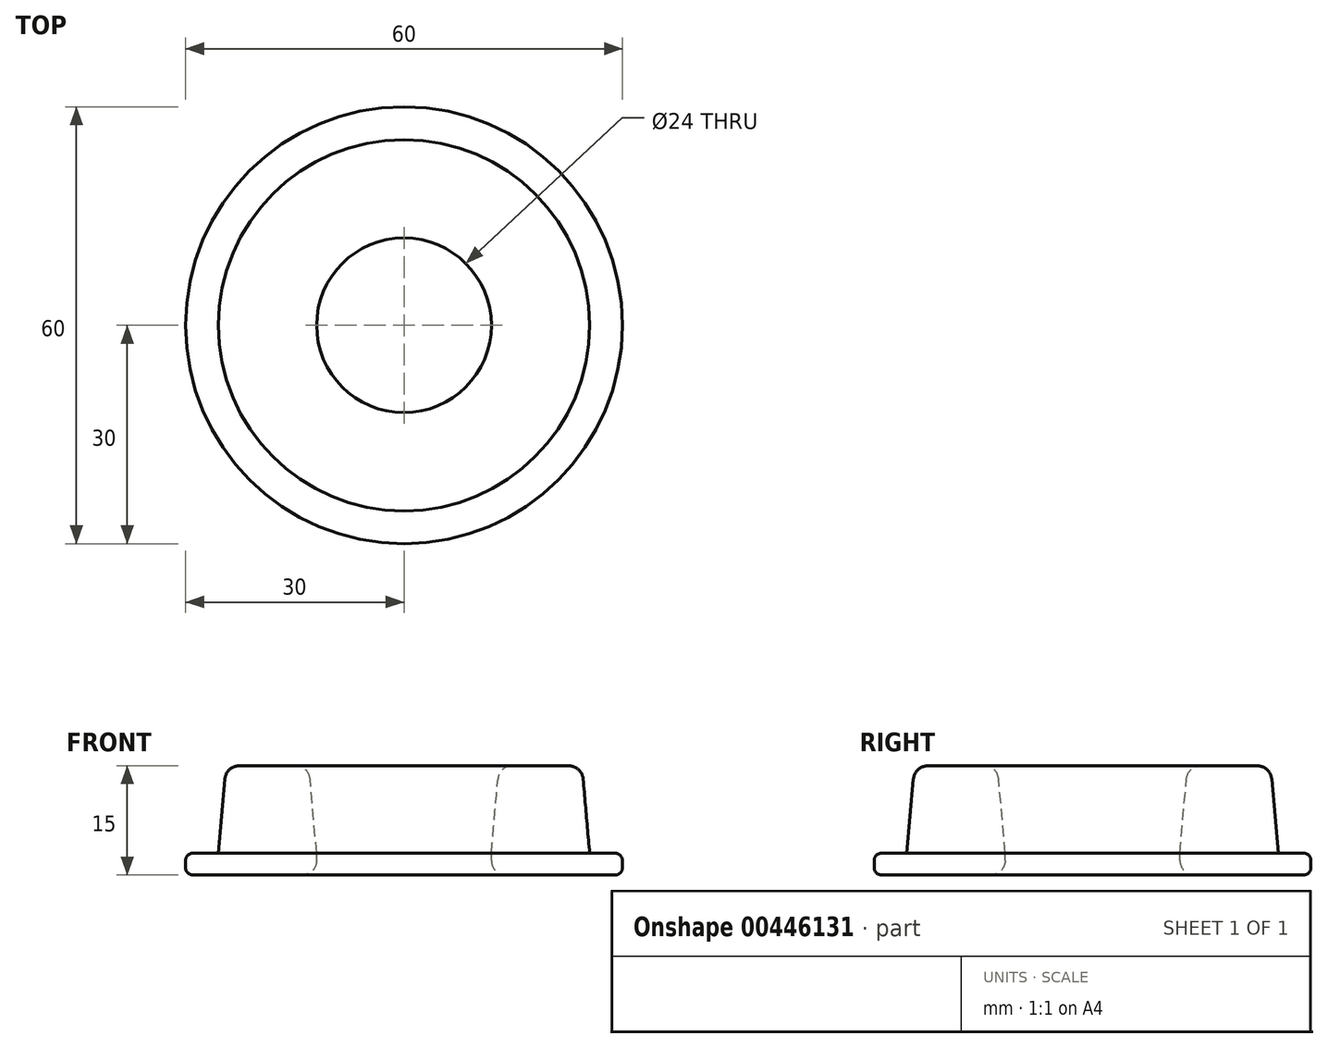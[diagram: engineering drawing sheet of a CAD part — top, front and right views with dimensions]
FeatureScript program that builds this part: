
annotation { "Feature Type Name" : "Feature", "Feature Type Description" : "" }
export const myFeature = defineFeature(function(context is Context, id is Id, definition is map)
    precondition{}
    {
        {
            var Q0;
            Q0=qCreatedBy(makeId("Top.planeOp"),FACE);
            var sketch = newSketch(context, id + "F0", { "sketchPlane" : qUnion([Q0])});
            skCircle(sketch, "E0", {"center": v(0, 0) * mm, "radius": 12 * mm});
            skCircle(sketch, "E1", {"center": v(0, 0) * mm, "radius": 25.5 * mm});
            skCircle(sketch, "E2", {"center": v(0, 0) * mm, "radius": 25.5 * mm, "construction": true});
            skSolve(sketch);
        }
        {
            var Q0;
            Q0=qSketchRegion(id+"F0",true);
            extrude(context, id + "F1", {"entities" : qUnion([Q0]), "depth" : 12 * mm, "hasDraft" : true, "draftAngle" : 5 * degree, "draftPullDirection" : true});
        }
        {
            var Q0;
            Q0=qCreatedBy(makeId("Top.planeOp"),FACE);
            var sketch = newSketch(context, id + "F2", { "sketchPlane" : qUnion([Q0])});
            skCircle(sketch, "E3", {"center": v(0, 0) * mm, "radius": 30 * mm});
            skCircle(sketch, "E4", {"center": v(0, 0) * mm, "radius": 12 * mm});
            skSolve(sketch);
        }
        {
            var Q0;
            Q0=qSketchRegion(id+"F2",true);
            extrude(context, id + "F3", {"entities" : qUnion([Q0]), "operationType" : NewBodyOperationType.ADD, "oppositeDirection" : true, "depth" : 3 * mm});
        }
        {
            var Q0;
            Q0=makeQuery(id+"F1.opExtrude","CAP_EDGE",EDGE,{"disambiguationData":[OSD([sQuery(id+"F0.wireOp",EDGE,"E1")])],"isStart":false});
            var Q1;
            Q1=makeQuery(id+"F3.opExtrude","CAP_EDGE",EDGE,{"disambiguationData":[OSD([sQuery(id+"F2.wireOp",EDGE,"E4")])],"isStart":false});
            var Q2;
            Q2=makeQuery(id+"F1.opExtrude","CAP_EDGE",EDGE,{"disambiguationData":[OSD([sQuery(id+"F0.wireOp",EDGE,"E0")])],"isStart":false});
            fillet(context, id + "F4", {"entities" : qUnion([Q0, Q1, Q2]), "radius" : 2 * mm, "tangentPropagation" : true, "allowEdgeOverflow" : false});
        }
        {
            var Q0;
            Q0=makeQuery(id+"F3.opExtrude","CAP_EDGE",EDGE,{"disambiguationData":[OSD([sQuery(id+"F2.wireOp",EDGE,"E3")])],"isStart":false});
            var Q1;
            Q1=makeQuery(id+"F3.opExtrude","CAP_EDGE",EDGE,{"disambiguationData":[OSD([sQuery(id+"F2.wireOp",EDGE,"E3")])],"isStart":true});
            fillet(context, id + "F5", {"entities" : qUnion([Q0, Q1]), "radius" : 1 * mm, "tangentPropagation" : true, "allowEdgeOverflow" : false});
        }
    });
